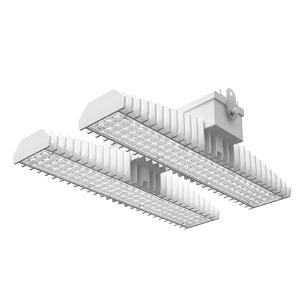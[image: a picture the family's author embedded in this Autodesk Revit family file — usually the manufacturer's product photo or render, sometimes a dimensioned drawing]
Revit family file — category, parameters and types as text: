
# Revit family: 3f_filippi_-_3f_lem_medio_3f_filippi_-_58893_a0811_-_3f_lem_2_led_100_cr_medio___vt_26c2
name_source: partatom
category: Lighting Fixtures
units: mm (PartAtom-declared; Revit-internal decimal feet)

## family parameters
Cut with Voids When Loaded = No
Host = Face
Light Source = No
Part Type = Normal
Room Calculation Point = No
Round Connector Dimension = Use Diameter
Shared = No

## types (1)
- 3F Filippi - 3F LEM Medio (1 x LED, 15479 lm, 109 W, 4000 K)
    Apparent Load = 109 VA
    Approval mark = CE
    CIE Flux Codes = 83 96 99 100 100
    Color Rendering = 80
    Color Temperature = 4000 K
    Control Gear = Electronic ballast
    Default Elevation = 1800 mm
    Description = Industrial luminaire with high light output and high luminous efficiency designed with the most innovative technologies for environments with temperature up to 55°C.

ILLUMINOTECHNICAL
Luminous efficiency 100% (DLOR 99%, ULOR 1%).
Initial luminous flux of the luminaire 15479 lm.
Medium distribution with rectangular shape.
Installation Interdistance Transv.D = 1.17 x hu - Long.D = 1.21 x hu.
Tabular UGR (CIE 117 - 4H-8H; S=0.25H; 70/50/20): RUG 18.2 - 17.8.
Beam angle: 65° - 67°.
Luminous efficacy 142 lm/W.
Lifetime (L93/B10): 30000 h. (tq+25°C)
Lifetime (L90/B10): 50000 h. (tq+25°C)
Lifetime (L85/B10): 80000 h. (tq+25°C)
Lifetime (L80/B10): 100000 h. (tq+25°C)
Lifetime (L85/B10): 50000 h. (tq+55°C)
Sudden decreased luminous flux after 50000 hours: 0% (C0).
Photobiological safety in compliance with IEC/TR 62778: RG0 risk exempt, (IEC 62471).
In compliance with IEC/EN 62722-2-1 - IEC/EN 62717 standards.

SOURCE
2 Mid-Power linear LED modules 50W/840.
Energy efficiency class (UE 2019/2020 - UE 2019/2015): C.
CIE 13.3 Colour rendering index: CRI >80 (R9 <50%).
IES TM-30 Fidelity Index: Rf = 84 Rg = 95.
CCT nominal colour temperature 4000 K.
Colour initial tolerance (MacAdam): SDCM 3.

MECHANICAL
Passive modular heatsinks in die-casted aluminium, painted in white colour.
To optimize the thermal management of the LED module, the heatsinks are oversized and provided with self-cleaning of cooling fins.
Wiring body in aluminium and galvanised steel anchored solidly to the sinks and thermally separated.
3F Lens lenses with high luminous efficiency, transparent methacrylate (PMMA), fixed to the LED modules.
Fixing brackets in stainless steel.
Luminaire with limited surface temperature. - D - (EN 60598-2-24)
Dimensions: 470x542 mm, height 133 mm. Weight 10.124 kg.
IP65 protection degree.
Mechanical strength to impacts IK06 (1 joule).
Glow-wire test resistance 650°C.

ELECTRICAL
Halogen Free electronic wiring 230V-50/60Hz, power factor 0.97, THD <25%, constant output current, class I, 1 driver.
Power of the luminaire 109 W.
ENEC - CE.
SAFE FLICKER: PstLM=<1 and SVM=<0.4 (IEC TR 61547-1 and IEC TR 63158), to ensure a more comfortable and safe light.
Luminaire compliant with EN 60598-2-22 for power supply from a centralised emergency system CPSS (Central Power Supply System), not incorporated in the luminaire - high risk areas excluded. The default power and flux are 100% in AC and 100% in DC.
Ambient temperature from -30°C to +55°C.
Temperature class T6 max 85°C.
Quick connection via M20 3P connector with 9-13 mm tightening range.
Power unit positioned on a separate compartment by the LED module to ensure optimum temperatures of cabling components, to be inspectable and maintainable.
Relative humidity UR: <85%.

INSTALLATION
Ceiling / Suspended / Wall.
All accessories dedicated to this product are available on the Catalog and on our website www.3F-Filippi.com.

ACCESSORIES
A0811 - VT transparent glass, tempered, not flammable, with sealing gasket.
One required for each light module. The pack contains 10 pieces.

APPLICATIONS
In commercial environments, exhibition and industrial areas, stores, open areas.
Applications with high ambient temperature up to 55°C.
Environments in which it is necessary a total protection against falling fragments (eg environments with foodstuffs or machines with moving parts or with extreme temperature changes), use luminaires with polycarbonate lenses.

WARNING
Fixture not suitable for cold stores with an ambient temperature <0°C and/or relative humidity >85%.
Luminaire designed for disposal/recycling at end-of-life.
Replaceable (LED only) light source by a professional. Replaceable control gear by a professional.
    Height = 133 mm  [stored 0.436352 ft]
    Lamp = 1 x LED
    Lamp Light Flux = 15479 lm
    Lamp Power = 109 W
    Lamp count = 1
    Length = 470 mm
    Lifetime = 50000 h
    Luminous efficacy = 142 lm/W
    Manufacturer = 3F Filippi
    ModVariant = No
    Model = 3F Filippi - 58893+A0811 - 3F LEM 2 LED 100 CR MEDIO + VT
    Mounting Place = Ceiling
    Mounting Type = Pendant
    Number of Poles = 1
    OnlyDefault = Yes
    Power Factor = 1
    Product Name = 3F Filippi - 3F LEM Medio
    Product group = pendant luminaire
    ProductGroupID = 9
    Protection Class = Protection class I
    Protection Degree = IP 65
    RLX_Detail_Level = 1
    RLX_Emergency_Light_Flux = 0 lm
    RLX_Emergency_Type = 0
    RLX_Emergency_Type_DB = No
    RlxData = <blob elided: 102337 chars, md5=bc797a4b>
    Socket = socket
    Standby Power = 0 W
    System Light Flux = 15479 lm
    System Power = 109 W
    Type Comments = Product without accessories
    Type Image = 3f_filippi_-_lem_2__a0811.jpg
    URL = http://relux.com
    VarID = ---
    Voltage = 0 V
    Weight = 0.00 kg
    Width = 542 mm

note: [stored X ft] marks values corroborated as IEEE doubles in the binary element streams (Revit-internal decimal feet)

## geometry (parser evidence)
native form markers: Blend x4, Sweep x10
no freeform markers — native parametric forms only
